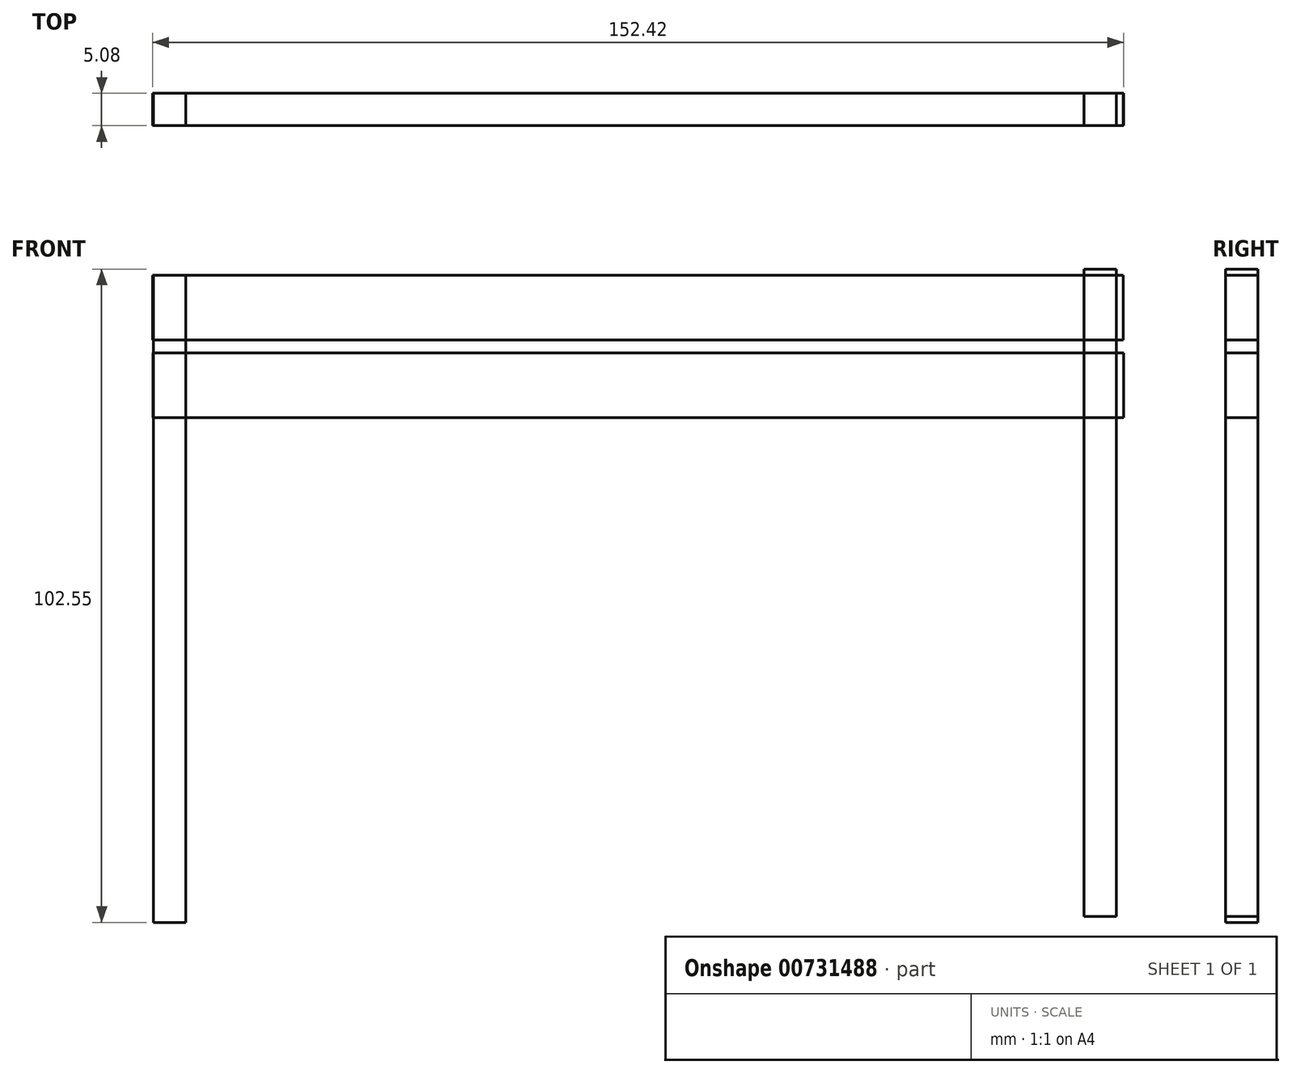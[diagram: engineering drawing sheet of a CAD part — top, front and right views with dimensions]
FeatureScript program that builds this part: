
annotation { "Feature Type Name" : "Feature", "Feature Type Description" : "" }
export const myFeature = defineFeature(function(context is Context, id is Id, definition is map)
    precondition{}
    {
        {
            var Q0;
            Q0=qCreatedBy(makeId("Front.planeOp"), FACE);
            var sketch = newSketch(context, id + "F0", { "sketchPlane" : qUnion([Q0])});
            skLineSegment(sketch, "E0.bottom", {"start": v(-75.97, 50.4) * mm, "end": v(-70.89, 50.4) * mm});
            skLineSegment(sketch, "E0.top", {"start": v(-75.97, -51.2) * mm, "end": v(-70.89, -51.2) * mm});
            skLineSegment(sketch, "E0.left", {"start": v(-75.97, 50.4) * mm, "end": v(-75.97, -51.2) * mm});
            skLineSegment(sketch, "E0.right", {"start": v(-70.89, 50.4) * mm, "end": v(-70.89, -51.2) * mm});
            skLineSegment(sketch, "E1.bottom", {"start": v(70.11, 51.35) * mm, "end": v(75.2, 51.35) * mm});
            skLineSegment(sketch, "E1.top", {"start": v(70.11, -50.25) * mm, "end": v(75.2, -50.25) * mm});
            skLineSegment(sketch, "E1.left", {"start": v(70.11, 51.35) * mm, "end": v(70.11, -50.25) * mm});
            skLineSegment(sketch, "E1.right", {"start": v(75.2, 51.35) * mm, "end": v(75.2, -50.25) * mm});
            skSolve(sketch);
        }
        {
            var Q0;
            Q0 = qSketchRegion(id + "F0", true);
            extrude(context, id + "F1", {"entities" : qUnion([Q0]), "depth" : 5.08 * mm, "offsetDistance" : 25.4 * mm});
        }
        {
            var Q0;
            Q0 = qSketchRegion(id + "F0", true);
            extrude(context, id + "F2", {"entities" : qUnion([Q0]), "depth" : 5.08 * mm, "offsetDistance" : 25.4 * mm});
        }
        {
            var Q0;
            Q0=qCreatedBy(makeId("Front.planeOp"), FACE);
            var sketch = newSketch(context, id + "F3", { "sketchPlane" : qUnion([Q0])});
            skLineSegment(sketch, "E2.bottom", {"start": v(-76.08, 50.35) * mm, "end": v(76.32, 50.35) * mm});
            skLineSegment(sketch, "E2.top", {"start": v(-76.08, 40.19) * mm, "end": v(76.32, 40.19) * mm});
            skLineSegment(sketch, "E2.left", {"start": v(-76.08, 50.35) * mm, "end": v(-76.08, 40.19) * mm});
            skLineSegment(sketch, "E2.right", {"start": v(76.32, 50.35) * mm, "end": v(76.32, 40.19) * mm});
            skLineSegment(sketch, "E3.bottom", {"start": v(-76.06, 38.16) * mm, "end": v(76.34, 38.16) * mm});
            skLineSegment(sketch, "E3.top", {"start": v(-76.06, 28) * mm, "end": v(76.34, 28) * mm});
            skLineSegment(sketch, "E3.left", {"start": v(-76.06, 38.16) * mm, "end": v(-76.06, 28) * mm});
            skLineSegment(sketch, "E3.right", {"start": v(76.34, 38.16) * mm, "end": v(76.34, 28) * mm});
            skSolve(sketch);
        }
        {
            var Q0;
            Q0 = qSketchRegion(id + "F3", true);
            extrude(context, id + "F4", {"entities" : qUnion([Q0]), "depth" : 5.08 * mm, "offsetDistance" : 25.4 * mm});
        }
    });
